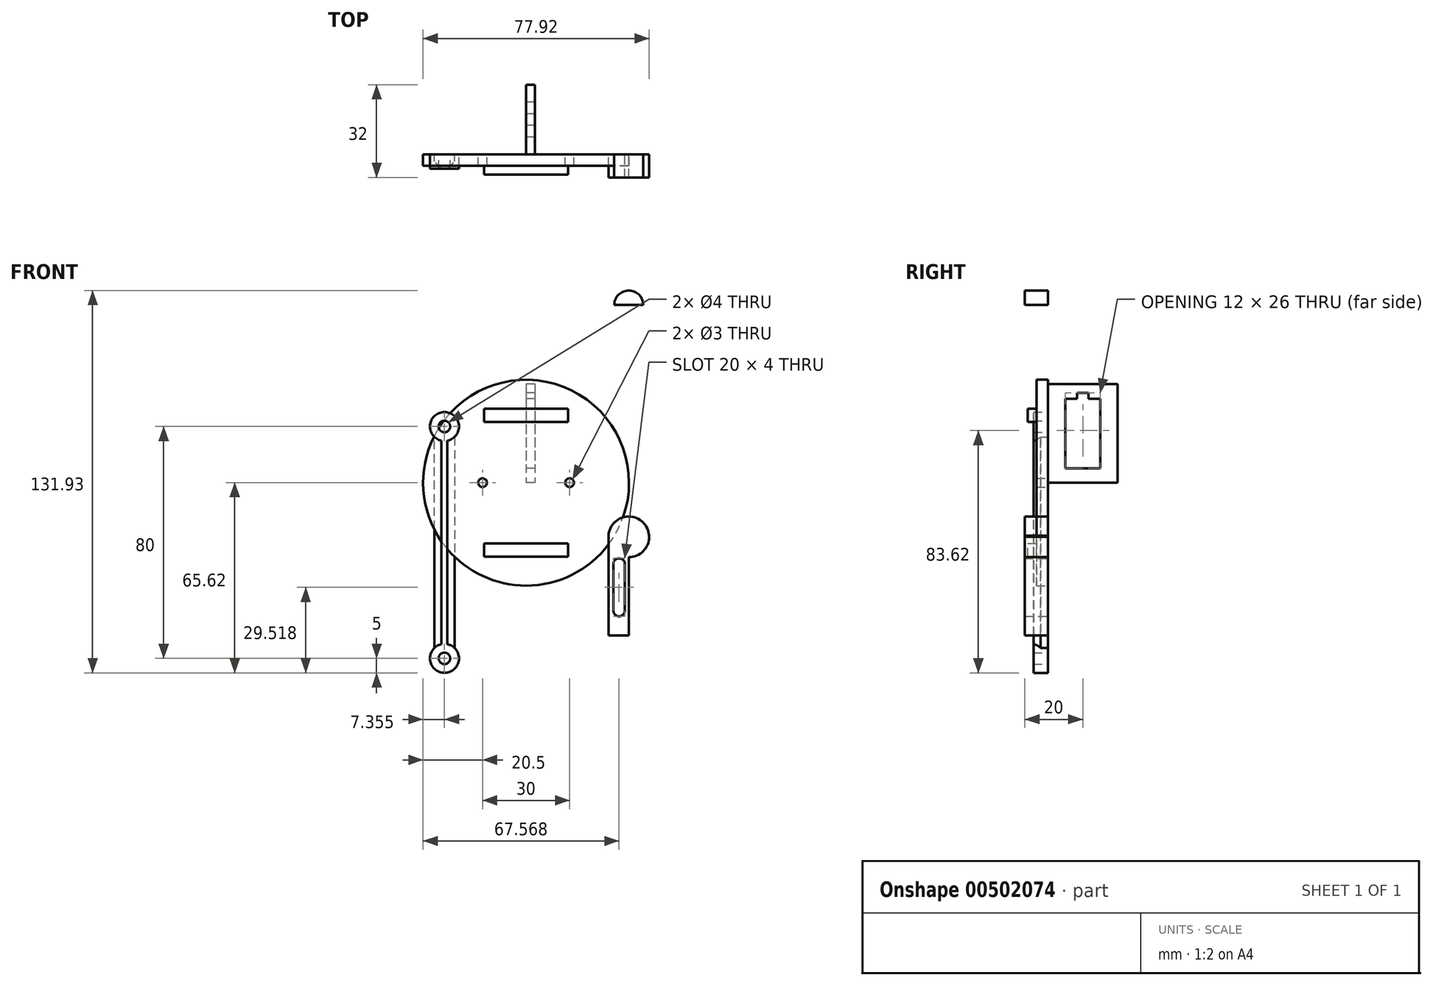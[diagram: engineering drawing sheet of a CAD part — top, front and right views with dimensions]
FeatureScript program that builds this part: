
annotation { "Feature Type Name" : "Feature", "Feature Type Description" : "" }
export const myFeature = defineFeature(function(context is Context, id is Id, definition is map)
    precondition{}
    {
        {
            var Q0;
            Q0=qCreatedBy(makeId("Front.planeOp"),FACE);
            var sketch = newSketch(context, id + "F0", { "sketchPlane" : qUnion([Q0])});
            skCircle(sketch, "E0", {"center": v(0, 0) * mm, "radius": 35.5 * mm});
            skLineSegment(sketch, "E1", {"start": v(0, 21) * mm, "end": v(-14.5, 21) * mm});
            skLineSegment(sketch, "E2", {"start": v(-14.5, 21) * mm, "end": v(-14.5, 25.5) * mm});
            skLineSegment(sketch, "E3", {"start": v(-14.5, 25.5) * mm, "end": v(14.5, 25.5) * mm});
            skLineSegment(sketch, "E4", {"start": v(14.5, 25.5) * mm, "end": v(14.5, 21) * mm});
            skLineSegment(sketch, "E5", {"start": v(14.5, 21) * mm, "end": v(0, 21) * mm});
            skLineSegment(sketch, "E6.MirrorCS", {"start": v(14.5, -25.5) * mm, "end": v(14.5, -21) * mm});
            skLineSegment(sketch, "E7.MirrorCS", {"start": v(14.5, -21) * mm, "end": v(0, -21) * mm});
            skLineSegment(sketch, "E8.MirrorCS", {"start": v(0, -21) * mm, "end": v(-14.5, -21) * mm});
            skLineSegment(sketch, "E9.MirrorCS", {"start": v(-14.5, -21) * mm, "end": v(-14.5, -25.5) * mm});
            skLineSegment(sketch, "E10.MirrorCS", {"start": v(-14.5, -25.5) * mm, "end": v(14.5, -25.5) * mm});
            skCircle(sketch, "E11", {"center": v(15, 0) * mm, "radius": 1.5 * mm});
            skCircle(sketch, "E12.MirrorC", {"center": v(-15, 0) * mm, "radius": 1.5 * mm});
            skSolve(sketch);
        }
        {
            var Q0;
            Q0=makeQuery(id+"F0.imprint","IMPRINT",FACE,{"disambiguationData":[TD([[makeQuery(id+"F0.imprint","IMPRINT",EDGE,{"derivedFrom":sQuery(id+"F0.wireOp",EDGE,"E0")}),1.0]])]});
            extrude(context, id + "F1", {"entities" : qUnion([Q0]), "depth" : 4 * mm});
        }
        {
            var Q0;
            Q0=makeQuery(id+"F0.imprint","IMPRINT",FACE,{"disambiguationData":[TD([[makeQuery(id+"F0.imprint","IMPRINT",EDGE,{"derivedFrom":sQuery(id+"F0.wireOp",EDGE,"E6.MirrorCS")}),1.0]])]});
            var Q1;
            Q1=makeQuery(id+"F0.imprint","IMPRINT",FACE,{"disambiguationData":[TD([[makeQuery(id+"F0.imprint","IMPRINT",EDGE,{"derivedFrom":sQuery(id+"F0.wireOp",EDGE,"E1")}),-1.0]])]});
            extrude(context, id + "F2", {"entities" : qUnion([Q0, Q1]), "operationType" : NewBodyOperationType.ADD, "depth" : 7 * mm});
        }
        {
            var Q0;
            Q0=qCreatedBy(makeId("Right.planeOp"),FACE);
            var sketch = newSketch(context, id + "F3", { "sketchPlane" : qUnion([Q0])});
            skLineSegment(sketch, "E13", {"start": v(0, 0) * mm, "end": v(24, 0) * mm});
            skLineSegment(sketch, "E14", {"start": v(24, 0) * mm, "end": v(24, 34) * mm});
            skLineSegment(sketch, "E15", {"start": v(24, 34) * mm, "end": v(0, 34) * mm});
            skLineSegment(sketch, "E16", {"start": v(0, 34) * mm, "end": v(0, 0) * mm});
            skLineSegment(sketch, "E17", {"start": v(6, 29) * mm, "end": v(6, 5) * mm});
            skLineSegment(sketch, "E18", {"start": v(6, 5) * mm, "end": v(18, 5) * mm});
            skLineSegment(sketch, "E19", {"start": v(18, 5) * mm, "end": v(18, 29) * mm});
            skLineSegment(sketch, "E20", {"start": v(18, 29) * mm, "end": v(14, 29) * mm});
            skLineSegment(sketch, "E21", {"start": v(14, 29) * mm, "end": v(14, 31) * mm});
            skLineSegment(sketch, "E22", {"start": v(14, 31) * mm, "end": v(10, 31) * mm});
            skLineSegment(sketch, "E23", {"start": v(10, 31) * mm, "end": v(10, 29) * mm});
            skLineSegment(sketch, "E24", {"start": v(10, 29) * mm, "end": v(6, 29) * mm});
            skSolve(sketch);
        }
        {
            var Q0;
            Q0=qCreatedBy(makeId("Front.planeOp"),FACE);
            var sketch = newSketch(context, id + "F4", { "sketchPlane" : qUnion([Q0])});
            skLineSegment(sketch, "E25.bottom", {"start": v(-31.64, 19.38) * mm, "end": v(-24.64, 19.38) * mm});
            skLineSegment(sketch, "E25.top", {"start": v(-31.64, -60.62) * mm, "end": v(-24.64, -60.62) * mm});
            skLineSegment(sketch, "E25.left", {"start": v(-31.64, 19.38) * mm, "end": v(-31.64, -60.62) * mm});
            skLineSegment(sketch, "E25.right", {"start": v(-24.64, 19.38) * mm, "end": v(-24.64, -60.62) * mm});
            skLineSegment(sketch, "E26", {"start": v(-31.64, 19.38) * mm, "end": v(-28.14, 19.38) * mm});
            skCircle(sketch, "E27", {"center": v(-28.14, 19.38) * mm, "radius": 5 * mm});
            skLineSegment(sketch, "E28", {"start": v(-31.64, -60.62) * mm, "end": v(-28.14, -60.62) * mm});
            skCircle(sketch, "E29", {"center": v(-28.14, -60.62) * mm, "radius": 5 * mm});
            skSolve(sketch);
        }
        {
            var Q0;
            {var subQ1=sQuery(id+"F4.wireOp",EDGE,"E25.top");Q0=makeQuery(id+"F4.imprint","IMPRINT",FACE,{"disambiguationData":[TD([[makeQuery(id+"F4.imprint","IMPRINT",EDGE,{"derivedFrom":subQ1}),1.0]])]});}
            var Q1;
            {var subQ0=sQuery(id+"F4.wireOp",EDGE,"E27");var subQ1=sQuery(id+"F4.wireOp",EDGE,"E25.left");var subQ2=makeQuery(id+"F4.imprint","INTERSECT",VERTEX,{"derivedFrom":[subQ1,subQ0]});Q1=makeQuery(id+"F4.imprint","IMPRINT",FACE,{"disambiguationData":[TD([[makeQuery(id+"F4.imprint","IMPRINT",EDGE,{"disambiguationData":[TD([[subQ2,-1.0]])],"derivedFrom":subQ1}),1.0]])]});}
            var Q2;
            {var subQ5=sQuery(id+"F4.wireOp",EDGE,"E25.bottom");Q2=makeQuery(id+"F4.imprint","IMPRINT",FACE,{"disambiguationData":[TD([[makeQuery(id+"F4.imprint","IMPRINT",EDGE,{"derivedFrom":subQ5}),1.0]])]});}
            var Q3;
            {var subQ5=sQuery(id+"F4.wireOp",EDGE,"E25.bottom");Q3=makeQuery(id+"F4.imprint","IMPRINT",FACE,{"disambiguationData":[TD([[makeQuery(id+"F4.imprint","IMPRINT",EDGE,{"derivedFrom":subQ5}),-1.0]])]});}
            var Q4;
            {var subQ1=sQuery(id+"F4.wireOp",EDGE,"E25.top");Q4=makeQuery(id+"F4.imprint","IMPRINT",FACE,{"disambiguationData":[TD([[makeQuery(id+"F4.imprint","IMPRINT",EDGE,{"derivedFrom":subQ1}),-1.0]])]});}
            extrude(context, id + "F5", {"entities" : qUnion([Q0, Q1, Q2, Q3, Q4]), "depth" : 5 * mm, "offsetDistance" : 25 * mm});
        }
        {
            var Q0;
            Q0=makeQuery(id+"F5.opExtrude","CAP_EDGE",EDGE,{"disambiguationData":[OSD([sQuery(id+"F4.wireOp",EDGE,"E25.left")])],"isStart":false});
            var Q1;
            Q1=makeQuery(id+"F5.opExtrude","CAP_EDGE",EDGE,{"disambiguationData":[OSD([sQuery(id+"F4.wireOp",EDGE,"E25.right")])],"isStart":false});
            chamfer(context, id + "F6", {"entities" : qUnion([Q0, Q1]), "width" : 2.5 * mm, "tangentPropagation" : true});
        }
        {
            var Q0;
            Q0=sQuery(id+"F4.wireOp",VERTEX,"E27.center");
            var Q1;
            Q1=sQuery(id+"F4.wireOp",VERTEX,"E29.center");
            var Q2;
            Q2=makeQuery(id+"F5.opExtrude","SWEPT_BODY",BODY,{"disambiguationData":[OSD([sQuery(id+"F4.wireOp",EDGE,"E25.left"),sQuery(id+"F4.wireOp",EDGE,"E25.right"),sQuery(id+"F4.wireOp",EDGE,"E27"),sQuery(id+"F4.wireOp",EDGE,"E29")])]});
            hole(context, id + "F7", {"style" : HoleStyle.C_BORE, "endStyle" : HoleEndStyle.BLIND, "oppositeDirection" : true, "holeDiameter" : 4 * mm, "cBoreDiameter" : 6 * mm, "cBoreDepth" : 0 * mm, "holeDepth" : 6 * mm, "isTappedThrough" : true, "tappedDepth" : 12 * mm, "tapClearance" : 3, "locations" : qUnion([Q0, Q1]), "scope" : qUnion([Q2])});
        }
        {
            var Q0;
            Q0=makeQuery(id+"F3.imprint","IMPRINT",FACE,{"disambiguationData":[TD([[makeQuery(id+"F3.imprint","IMPRINT",EDGE,{"derivedFrom":sQuery(id+"F3.wireOp",EDGE,"E13")}),1.0]])]});
            extrude(context, id + "F8", {"entities" : qUnion([Q0]), "depth" : 3 * mm, "offsetDistance" : 25 * mm});
        }
        {
            var Q0;
            Q0=qCreatedBy(makeId("Front.planeOp"),FACE);
            var sketch = newSketch(context, id + "F9", { "sketchPlane" : qUnion([Q0])});
            skLineSegment(sketch, "E30", {"start": v(35.42, 61.31) * mm, "end": v(35.42, -52.69) * mm});
            skLineSegment(sketch, "E31", {"start": v(35.42, 61.31) * mm, "end": v(35.42, -18.69) * mm});
            skCircle(sketch, "E32", {"center": v(35.42, 61.31) * mm, "radius": 5 * mm});
            skCircle(sketch, "E33", {"center": v(35.42, -18.69) * mm, "radius": 7 * mm});
            skCircle(sketch, "E34", {"center": v(35.42, -52.69) * mm, "radius": 7 * mm});
            skLineSegment(sketch, "E35", {"start": v(35.42, 61.31) * mm, "end": v(40.42, 61.31) * mm});
            skLineSegment(sketch, "E36", {"start": v(40.42, 61.31) * mm, "end": v(30.42, 61.31) * mm});
            skLineSegment(sketch, "E37", {"start": v(35.42, -18.69) * mm, "end": v(42.42, -18.69) * mm});
            skLineSegment(sketch, "E38", {"start": v(42.42, -18.69) * mm, "end": v(28.42, -18.69) * mm});
            skLineSegment(sketch, "E39", {"start": v(35.42, -52.69) * mm, "end": v(42.42, -52.69) * mm});
            skLineSegment(sketch, "E40", {"start": v(42.42, -52.69) * mm, "end": v(35.42, -52.69) * mm});
            skLineSegment(sketch, "E41", {"start": v(35.42, -52.69) * mm, "end": v(28.42, -52.69) * mm});
            skLineSegment(sketch, "E42", {"start": v(30.42, 61.31) * mm, "end": v(28.42, -18.69) * mm});
            skLineSegment(sketch, "E43", {"start": v(28.42, -18.69) * mm, "end": v(28.42, -52.69) * mm});
            skLineSegment(sketch, "E44", {"start": v(42.42, -18.69) * mm, "end": v(40.42, 61.31) * mm});
            skLineSegment(sketch, "E45", {"start": v(35.42, -11.69) * mm, "end": v(35.42, -6.94) * mm});
            skCircle(sketch, "E46", {"center": v(35.42, -6.94) * mm, "radius": 4.75 * mm});
            skLineSegment(sketch, "E47", {"start": v(35.42, 56.31) * mm, "end": v(35.42, 52.58) * mm});
            skLineSegment(sketch, "E48", {"start": v(35.42, 52.58) * mm, "end": v(35.42, 47.58) * mm});
            skCircle(sketch, "E49", {"center": v(35.42, 47.58) * mm, "radius": 2.5 * mm});
            skLineSegment(sketch, "E50", {"start": v(35.42, 47.58) * mm, "end": v(37.92, 47.58) * mm});
            skLineSegment(sketch, "E51", {"start": v(37.92, 47.58) * mm, "end": v(32.92, 47.58) * mm});
            skLineSegment(sketch, "E52", {"start": v(35.42, -6.94) * mm, "end": v(40.17, -7.06) * mm});
            skLineSegment(sketch, "E53", {"start": v(35.42, -6.94) * mm, "end": v(30.67, -6.94) * mm});
            skLineSegment(sketch, "E54", {"start": v(30.67, -6.94) * mm, "end": v(32.92, 47.58) * mm});
            skLineSegment(sketch, "E55", {"start": v(37.92, 47.58) * mm, "end": v(40.17, -7.06) * mm});
            skLineSegment(sketch, "E56", {"start": v(35.42, -25.69) * mm, "end": v(35.42, -26.69) * mm});
            skLineSegment(sketch, "E57", {"start": v(35.42, -26.69) * mm, "end": v(35.42, -43.66) * mm});
            skCircle(sketch, "E58", {"center": v(32.07, -44.1) * mm, "radius": 2 * mm});
            skLineSegment(sketch, "E59", {"start": v(32.07, -44.1) * mm, "end": v(30.07, -44.1) * mm});
            skLineSegment(sketch, "E60", {"start": v(32.07, -44.1) * mm, "end": v(34.07, -44.1) * mm});
            skLineSegment(sketch, "E61", {"start": v(30.07, -44.1) * mm, "end": v(30.07, -28.1) * mm});
            skLineSegment(sketch, "E62", {"start": v(30.07, -28.1) * mm, "end": v(32.07, -28.1) * mm});
            skLineSegment(sketch, "E63", {"start": v(32.07, -28.1) * mm, "end": v(34.07, -28.1) * mm});
            skLineSegment(sketch, "E64", {"start": v(34.07, -28.1) * mm, "end": v(34.07, -44.1) * mm});
            skCircle(sketch, "E65", {"center": v(32.07, -28.1) * mm, "radius": 2 * mm});
            skSolve(sketch);
        }
        {
            var Q0;
            {var subQ11=sQuery(id+"F9.wireOp",EDGE,"E47");Q0=makeQuery(id+"F9.imprint","IMPRINT",FACE,{"disambiguationData":[TD([[makeQuery(id+"F9.imprint","IMPRINT",EDGE,{"derivedFrom":subQ11}),-1.0]])]});}
            var Q1;
            {var subQ0=sQuery(id+"F9.wireOp",EDGE,"E36");var subQ4=makeQuery(id+"F9.imprint","INTERSECT",VERTEX,{"derivedFrom":[sQuery(id+"F9.wireOp",EDGE,"E31"),subQ0]});Q1=makeQuery(id+"F9.imprint","IMPRINT",FACE,{"disambiguationData":[TD([[makeQuery(id+"F9.imprint","IMPRINT",EDGE,{"disambiguationData":[TD([[subQ4,1.0]])],"derivedFrom":subQ0}),-1.0]])]});}
            var Q2;
            {var subQ0=sQuery(id+"F9.wireOp",EDGE,"E36");var subQ1=sQuery(id+"F9.wireOp",EDGE,"E31");var subQ2=makeQuery(id+"F9.imprint","INTERSECT",VERTEX,{"derivedFrom":[subQ1,subQ0]});Q2=makeQuery(id+"F9.imprint","IMPRINT",FACE,{"disambiguationData":[TD([[makeQuery(id+"F9.imprint","IMPRINT",EDGE,{"disambiguationData":[TD([[subQ2,-1.0]])],"derivedFrom":subQ1}),-1.0]])]});}
            var Q3;
            {var subQ0=sQuery(id+"F9.wireOp",EDGE,"E36");var subQ1=sQuery(id+"F9.wireOp",EDGE,"E31");var subQ2=makeQuery(id+"F9.imprint","INTERSECT",VERTEX,{"derivedFrom":[subQ1,subQ0]});Q3=makeQuery(id+"F9.imprint","IMPRINT",FACE,{"disambiguationData":[TD([[makeQuery(id+"F9.imprint","IMPRINT",EDGE,{"disambiguationData":[TD([[subQ2,-1.0]])],"derivedFrom":subQ1}),1.0]])]});}
            var Q4;
            {var subQ14=sQuery(id+"F9.wireOp",EDGE,"E47");Q4=makeQuery(id+"F9.imprint","IMPRINT",FACE,{"disambiguationData":[TD([[makeQuery(id+"F9.imprint","IMPRINT",EDGE,{"derivedFrom":subQ14}),1.0]])]});}
            var Q5;
            {var subQ3=sQuery(id+"F9.wireOp",EDGE,"E33");var subQ5=sQuery(id+"F9.wireOp",EDGE,"E42");var subQ7=makeQuery(id+"F9.imprint","INTERSECT",VERTEX,{"derivedFrom":[subQ3,subQ5]});Q5=makeQuery(id+"F9.imprint","IMPRINT",FACE,{"disambiguationData":[TD([[makeQuery(id+"F9.imprint","IMPRINT",EDGE,{"disambiguationData":[TD([[subQ7,1.0]])],"derivedFrom":subQ3}),1.0]])]});}
            var Q6;
            {var subQ3=sQuery(id+"F9.wireOp",EDGE,"E33");var subQ5=sQuery(id+"F9.wireOp",EDGE,"E44");var subQ6=makeQuery(id+"F9.imprint","INTERSECT",VERTEX,{"derivedFrom":[subQ3,subQ5]});Q6=makeQuery(id+"F9.imprint","IMPRINT",FACE,{"disambiguationData":[TD([[makeQuery(id+"F9.imprint","IMPRINT",EDGE,{"disambiguationData":[TD([[subQ6,1.0]])],"derivedFrom":subQ5}),1.0]])]});}
            var Q7;
            {var subQ0=sQuery(id+"F9.wireOp",EDGE,"E38");var subQ1=sQuery(id+"F9.wireOp",EDGE,"E30");var subQ2=makeQuery(id+"F9.imprint","INTERSECT",VERTEX,{"derivedFrom":[subQ1,sQuery(id+"F9.wireOp",EDGE,"E31"),subQ0]});Q7=makeQuery(id+"F9.imprint","IMPRINT",FACE,{"disambiguationData":[TD([[makeQuery(id+"F9.imprint","IMPRINT",EDGE,{"disambiguationData":[TD([[subQ2,-1.0]])],"derivedFrom":subQ1}),1.0]])]});}
            var Q8;
            {var subQ0=sQuery(id+"F9.wireOp",EDGE,"E38");var subQ1=sQuery(id+"F9.wireOp",EDGE,"E30");var subQ2=makeQuery(id+"F9.imprint","INTERSECT",VERTEX,{"derivedFrom":[subQ1,sQuery(id+"F9.wireOp",EDGE,"E31"),subQ0]});Q8=makeQuery(id+"F9.imprint","IMPRINT",FACE,{"disambiguationData":[TD([[makeQuery(id+"F9.imprint","IMPRINT",EDGE,{"disambiguationData":[TD([[subQ2,-1.0]])],"derivedFrom":subQ1}),-1.0]])]});}
            var Q9;
            {var subQ0=sQuery(id+"F9.wireOp",EDGE,"E43");Q9=makeQuery(id+"F9.imprint","IMPRINT",FACE,{"disambiguationData":[TD([[makeQuery(id+"F9.imprint","IMPRINT",EDGE,{"derivedFrom":subQ0}),1.0]])]});}
            var Q10;
            {var subQ0=sQuery(id+"F9.wireOp",EDGE,"E41");Q10=makeQuery(id+"F9.imprint","IMPRINT",FACE,{"disambiguationData":[TD([[makeQuery(id+"F9.imprint","IMPRINT",EDGE,{"derivedFrom":subQ0}),-1.0]])]});}
            var Q11;
            {var subQ0=sQuery(id+"F9.wireOp",EDGE,"E40");Q11=makeQuery(id+"F9.imprint","IMPRINT",FACE,{"disambiguationData":[TD([[makeQuery(id+"F9.imprint","IMPRINT",EDGE,{"derivedFrom":subQ0}),-1.0]])]});}
            var Q12;
            {var subQ0=sQuery(id+"F9.wireOp",EDGE,"E40");Q12=makeQuery(id+"F9.imprint","IMPRINT",FACE,{"disambiguationData":[TD([[makeQuery(id+"F9.imprint","IMPRINT",EDGE,{"derivedFrom":subQ0}),1.0]])]});}
            extrude(context, id + "F10", {"entities" : qUnion([Q0, Q1, Q2, Q3, Q4, Q5, Q6, Q7, Q8, Q9, Q10, Q11, Q12]), "depth" : 8 * mm, "offsetDistance" : 25 * mm});
        }
    });
